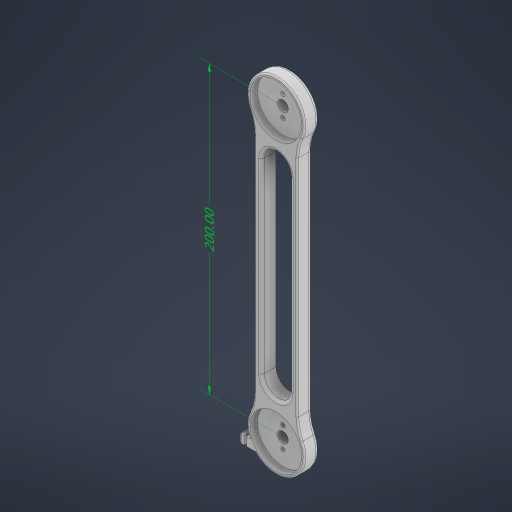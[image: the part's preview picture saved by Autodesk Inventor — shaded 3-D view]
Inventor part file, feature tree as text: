
AUTODESK INVENTOR PART (.ipt)
format: ipt  version: 2023 (Build 270158000, 158)  size: 333,312 bytes
history: native  units: mm
features: extrude x5, fillet x5, sketch x5, other x2
ambient origin geometry x8: Origin, YZ Plane, XZ Plane, XY Plane, X Axis, Y Axis, Z Axis, Center Point
bodies: Solid1 (feature_tree)
feature tree (17):
  other  "Annotations"
  extrude  "Extrusion1"  Depth=40.0mm
  extrude  "Extrusion2"  Depth=10.0mm TaperAngle=0.0deg
  extrude  "Extrusion3"  Depth=3.0mm
  extrude  "Extrusion4"  Depth=7.25mm
  fillet  "Fillet1"  Radius=7.25mm
  extrude  "Extrusion5"  Depth=1.0mm
  fillet  "Fillet2"  Radius=3.0mm
  fillet  "Fillet3"  Radius=7.25mm
  fillet  "Fillet4"  Radius=7.25mm
  fillet  "Fillet5"  Radius=10.0mm
  sketch  "Sketch1"  dims[d0=40.0mm d3=40.0mm]
  sketch  "Sketch2"  dims[d4=30.0mm d5=10.0mm d6=0.0mm]
  sketch  "Sketch3"  dims[d7=7.5mm d8=3.0mm]
  sketch  "Sketch4"  dims[d9=3.0mm d10=7.25mm d11=7.25mm]
  sketch  "Sketch6"  dims[d12=7.5mm d13=3.0mm d14=3.0mm d15=7.25mm d16=7.25mm d17=10.0mm d18=0.0mm d19=36.0mm d20=36.0mm d21=5.0mm d22=0.0mm d23=20.0mm d24=150.0mm d25=10.0mm d26=0.0mm d27=10.0mm d30=10.0mm d31=0.0mm d32=5.0mm d33=1.0mm d34=2.0mm d35=2.0mm d36=1.0mm d37=200.0mm]
  other  "Linear Dimension 1"
